# Revit family: IS_CeramixBlue_A5646_BIM_DE
name_source: partatom
category: Plumbing Fixtures
revit_build: Autodesk Revit MEP 2015 (Build: 20140606_1530(x64)
units: mm (PartAtom-declared; Revit-internal decimal feet)

## types (1)
- A5646AA - CERAMIX BLUE single lever one hole basin mixer with pop-up waste
    Assembly Code = C1030200
    BIMobject category = Taps & Mixers
    BOSUseNativeGeometries = 1
    Brand url = http://www.idealstandard.co.uk
    Description = A5646AA CERAMIX BLUE single lever one hole basin mixer with pop-up waste
    EAN code = https://4015413326285
    Edition number = 1
    FaucetFunction = mixed
    FaucetOperation = leverhandle
    FaucetType = pillar
    IFC Classification = BRASSWARE BASIN
    IfcExportAs = IfcValveType
    IfcExportType = BRASSWARE BASIN
    Installation instructions = http://www.idealspec.co.uk
    Manufacturer name = Ideal Standard
    ManufacturerURL = www.idealstandard.com
    Material = Brass
    Material main = Brass
    Model = A5646AA
    ModelNumber = A5646AA
    Name = CERAMIX BLUE single lever one hole basin mixer with pop-up waste
    NettWeight = 2,145 kg
    Nominal height = 153
    Nominal width = 0
    NominalDepth = 0 mm  [stored 0 ft]
    NominalHeight = 153 mm  [stored 0.501969 ft]
    NominalLength = 181 mm
    NominalWidth = 55 mm
    OmniClass Code = 23.45.55.17
    OmniClass Description = Mixing Faucets
    Product Guid = 887a3989-face-4121-880d-670b1cf2338f
    Product SKU = A5646
    Product data url = https://bimobject.com
    Product family = CERAMIX BLUE
    Product group = Basin Mixer
    Product name = CERAMIX BLUE - Basin Mixer Rim Pu/M T/Fix Spx
    Product url = http://www.idealspec.co.uk
    ProductInformation = www.idealstandard.de/produkte
    QR code = http://bimobject.com
    Shape = Sculptured
    Size = 153x181x55 mm
    Space = Internal
    SpareParts = www.idealstandard.de/ersatzteile
    Technical description = www.idealstandard.de/produkte
    TestPressure = 10 Bar
    URL = www.idealstandard.com
    Uniclass 2015 Code = Pr_40_20_87_98
    Uniclass 2015 Name = Washbasin taps
    Uniclass2015Code = Pr_40_20_87_98
    Uniclass2015Title = Washbasin taps
    ValveMechanism = ceramic disc
    ValveOperation = lever
    Version = 1
    VolumeUnits = Litres
    WarrantyDurationParts = 5
    WarrantyDurationUnit = year
    Weight Net (Kg) = 2.15
    WorkingPressure = 1-5 Bar

note: [stored X ft] marks values corroborated as IEEE doubles in the binary element streams (Revit-internal decimal feet)

## geometry (parser evidence)
native form markers: Blend x4, Sweep x1
no freeform markers — native parametric forms only
